# Revit family: DC_Holyoake_OutsideLouver_OHCL-F-124_supply_13
name_source: partatom
category: Air Terminals
revit_build: Autodesk Revit 2014 (Build: 20130308_1515(x64)
units: mm (PartAtom-declared; Revit-internal decimal feet)

## types (2) — shared parameters
Accessories = Aluminium Bird mesh or insect mesh (fibreglass)
Blade Height = 89.8 mm
Blade Offset = 4.63 mm
Blade Pitch = 76.2 mm  [stored 0.25 ft]
Blade Width = 97.1 mm  [stored 0.31857 ft]
Flange Width = 25.4 mm  [stored 0.0833333 ft]
Gang Bar Width (plus min. 300mm clearance) = 50 mm  [stored 0.164042 ft]
Gang Bar with Actuator Width (plus min. 300mm clearance) = 150 mm  [stored 0.492126 ft]
Louver Depth = 106.35 mm  [stored 0.348917 ft]
Manufacturer = Holyoake
Max Flow = 5000.0 L/s
Min Flow = 100.0 L/s
Overall Depth = 38.3 mm
Static Pressure Max = 60.0 Pa
Static Pressure Min = 10.0 Pa

## per-type parameters (varying)
| type | Blade Array Count | Blade Control | Blade Count | Blade Cut Setout | Blade Length | Connector Height | Connector Width | Description | Exact Neck Height | Exact Neck Width | Exact Overall Flange Height | Exact Overall Flange Width | Holyoake Product Range | Material - Body | Material - Face | Nominal Height | Nominal Width | Overall Opening | Top Blade Height | Type Comments | URL |
| OHL-F-124 | 10.669291 | No | 10 | 762 mm | 688 mm  [stored 2.25722 ft] | 789 mm | 664 mm  [stored 2.17848 ft] | Holyoake Outside Horizontal Louvre | 860 mm  [stored 2.82152 ft] | 735 mm  [stored 2.41142 ft] | 910.8 mm | 785.8 mm |  | <By Category> | <By Category> | 866 mm | 741 mm  [stored 2.4311 ft] | 813 mm  [stored 2.66732 ft] | 51 mm | 124mm Horizontal Curved Profile Louvers in Flanged Surround | http://www.productspec.net |
| OHCL-F-124 | 9.88189 | Yes | 9 | 685.8 mm | 700 mm  [stored 2.29659 ft] | 729 mm | 676 mm | Closable Weather Louvres shall be Holyoake Model OHCL-F-124 straight profile 100mm louvred blades set at 76mm centres and constructed in a 107mm flanged (F) frame to suit the installation profile. Each Blade shall be fitted with a concealed damper blade pivoted on the underside of each fixed blade which is gang operated by either manual or motorised means. Closable Weather Louvres shall be of extruded aluminium construction and finished in natural anodised or powdercoat and fitted with accessories and dampers where indicated as manufactured by Holyoake. | 800 mm  [stored 2.62467 ft] | 747 mm  [stored 2.45079 ft] | 850.8 mm | 797.8 mm | Outside Louvres | Holyoake Aluminium | Holyoake Aluminium | 806 mm | 753 mm  [stored 2.47047 ft] | 753 mm  [stored 2.47047 ft] | 67.2 mm | 124mm Closable Horizontal Louvers in Flanged Surround | http://www.holyoake.com |

note: column(s) folded — value = type name in every type: Model

note: [stored X ft] marks values corroborated as IEEE doubles in the binary element streams (Revit-internal decimal feet)

## geometry (parser evidence)
native form markers: Blend x10, Sweep x9
no freeform markers — native parametric forms only
